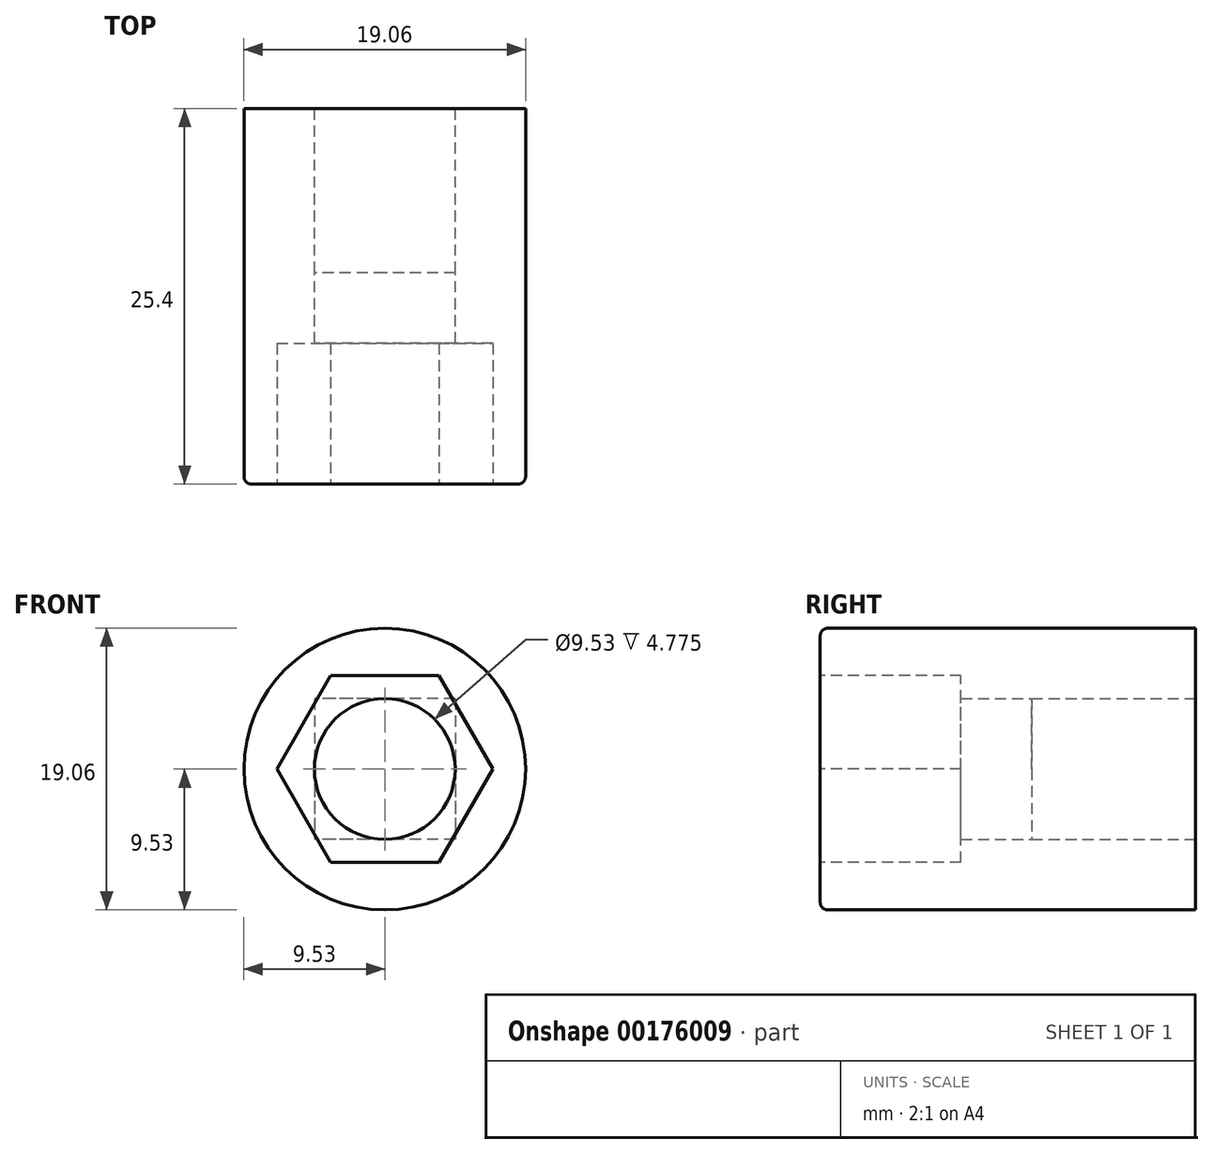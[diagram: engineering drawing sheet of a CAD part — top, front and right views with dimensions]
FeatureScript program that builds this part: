
annotation { "Feature Type Name" : "Feature", "Feature Type Description" : "" }
export const myFeature = defineFeature(function(context is Context, id is Id, definition is map)
    precondition{}
    {
        {
            var Q0;
            Q0=qCreatedBy(makeId("Front.planeOp"),FACE);
            var sketch = newSketch(context, id + "F0", { "sketchPlane" : qUnion([Q0])});
            skCircle(sketch, "E0", {"center": v(0, 0) * mm, "radius": 9.53 * mm});
            skSolve(sketch);
        }
        {
            var Q0;
            Q0=makeQuery(id+"F0.imprint","IMPRINT",FACE,{"disambiguationData":[TD([[makeQuery(id+"F0.imprint","IMPRINT",EDGE,{"derivedFrom":sQuery(id+"F0.wireOp",EDGE,"E0")}),1.0]])]});
            extrude(context, id + "F1", {"entities" : qUnion([Q0]), "depth" : 25.4 * mm});
        }
        {
            var Q0;
            Q0=qCreatedBy(makeId("Front.planeOp"),FACE);
            var sketch = newSketch(context, id + "F2", { "sketchPlane" : qUnion([Q0])});
            skLineSegment(sketch, "E1.bottom", {"start": v(4.76, 4.76) * mm, "end": v(-4.76, 4.76) * mm});
            skLineSegment(sketch, "E1.top", {"start": v(4.76, -4.76) * mm, "end": v(-4.76, -4.76) * mm});
            skLineSegment(sketch, "E1.left", {"start": v(4.76, 4.76) * mm, "end": v(4.76, -4.76) * mm});
            skLineSegment(sketch, "E1.right", {"start": v(-4.76, 4.76) * mm, "end": v(-4.76, -4.76) * mm});
            skPoint(sketch, "E1.middle", {"position": v(0, 0) * mm});
            skCircle(sketch, "E2", {"center": v(0, 0) * mm, "radius": 4.76 * mm});
            skSolve(sketch);
        }
        {
            var Q0;
            {var subQ0=sQuery(id+"F2.wireOp",EDGE,"E2");var subQ1=makeQuery(id+"F2.imprint","INTERSECT",VERTEX,{"derivedFrom":[sQuery(id+"F2.wireOp",EDGE,"E1.bottom"),subQ0]});Q0=makeQuery(id+"F2.imprint","IMPRINT",FACE,{"disambiguationData":[TD([[makeQuery(id+"F2.imprint","IMPRINT",EDGE,{"disambiguationData":[TD([[subQ1,1.0]])],"derivedFrom":subQ0}),1.0]])]});}
            extrude(context, id + "F3", {"entities" : qUnion([Q0]), "operationType" : NewBodyOperationType.REMOVE, "endBound" : BoundingType.THROUGH_ALL, "oppositeDirection" : true, "depth" : 25.4 * mm});
        }
        {
            var Q0;
            Q0=makeQuery(id+"F1.opExtrude","CAP_FACE",FACE,{"disambiguationData":[OSD([sQuery(id+"F0.wireOp",EDGE,"E0")])],"isStart":true});
            var sketch = newSketch(context, id + "F4", { "sketchPlane" : qUnion([Q0])});
            skLineSegment(sketch, "E3.bottom", {"start": v(4.76, -4.76) * mm, "end": v(-4.76, -4.76) * mm});
            skLineSegment(sketch, "E3.top", {"start": v(4.76, 4.76) * mm, "end": v(-4.76, 4.76) * mm});
            skLineSegment(sketch, "E3.left", {"start": v(4.76, -4.76) * mm, "end": v(4.76, 4.76) * mm});
            skLineSegment(sketch, "E3.right", {"start": v(-4.76, -4.76) * mm, "end": v(-4.76, 4.76) * mm});
            skPoint(sketch, "E3.middle", {"position": v(0, 0) * mm});
            skCircle(sketch, "E4", {"center": v(0, 0) * mm, "radius": 4.76 * mm});
            skSolve(sketch);
        }
        {
            var Q0;
            {var subQ0=sQuery(id+"F4.wireOp",EDGE,"E4");var subQ1=makeQuery(id+"F4.imprint","INTERSECT",VERTEX,{"derivedFrom":[sQuery(id+"F4.wireOp",EDGE,"E3.top"),subQ0]});Q0=makeQuery(id+"F4.imprint","IMPRINT",FACE,{"disambiguationData":[TD([[makeQuery(id+"F4.imprint","IMPRINT",EDGE,{"disambiguationData":[TD([[subQ1,1.0]])],"derivedFrom":subQ0}),1.0]])]});}
            extrude(context, id + "F5", {"entities" : qUnion([Q0]), "operationType" : NewBodyOperationType.REMOVE, "endBound" : BoundingType.THROUGH_ALL, "oppositeDirection" : true, "depth" : 25.4 * mm});
        }
        {
            var Q0;
            Q0 = qSketchRegion(id + "F2", true);
            extrude(context, id + "F6", {"entities" : qUnion([Q0]), "operationType" : NewBodyOperationType.REMOVE, "oppositeDirection" : true, "depth" : 9.4 * mm});
        }
        {
            var Q0;
            Q0 = qSketchRegion(id + "F2", true);
            extrude(context, id + "F7", {"entities" : qUnion([Q0]), "operationType" : NewBodyOperationType.REMOVE, "oppositeDirection" : true, "depth" : 12.7 * mm});
        }
        {
            var Q0;
            Q0 = qSketchRegion(id + "F2", true);
            extrude(context, id + "F8", {"entities" : qUnion([Q0]), "operationType" : NewBodyOperationType.REMOVE, "depth" : 11.1 * mm});
        }
        {
            var Q0;
            Q0=makeQuery(id+"F1.opExtrude","CAP_FACE",FACE,{"disambiguationData":[OSD([sQuery(id+"F0.wireOp",EDGE,"E0")])],"isStart":false});
            var sketch = newSketch(context, id + "F9", { "sketchPlane" : qUnion([Q0])});
            skCircle(sketch, "E5.cCircle", {"center": v(0, 0) * mm, "radius": 6.32 * mm, "construction": true});
            skLineSegment(sketch, "E5.0", {"start": v(-3.65, 6.32) * mm, "end": v(3.65, 6.32) * mm});
            skLineSegment(sketch, "E5.1", {"start": v(3.65, 6.32) * mm, "end": v(7.3, 0) * mm});
            skLineSegment(sketch, "E5.2", {"start": v(7.3, 0) * mm, "end": v(3.65, -6.32) * mm});
            skLineSegment(sketch, "E5.3", {"start": v(3.65, -6.32) * mm, "end": v(-3.65, -6.32) * mm});
            skLineSegment(sketch, "E5.4", {"start": v(-3.65, -6.32) * mm, "end": v(-7.3, 0) * mm});
            skLineSegment(sketch, "E5.5", {"start": v(-7.3, 0) * mm, "end": v(-3.65, 6.32) * mm});
            skPoint(sketch, "E5.0.midPoint", {"position": v(0, 6.32) * mm});
            skSolve(sketch);
        }
        {
            var Q0;
            Q0 = qSketchRegion(id + "F9", true);
            extrude(context, id + "F10", {"entities" : qUnion([Q0]), "operationType" : NewBodyOperationType.REMOVE, "oppositeDirection" : true, "depth" : 9.52 * mm});
        }
        {
            var Q0;
            Q0=makeQuery(id+"F1.opExtrude","CAP_EDGE",EDGE,{"disambiguationData":[OSD([sQuery(id+"F0.wireOp",EDGE,"E0")])],"isStart":false});
            var Q1;
            Q1=makeQuery(id+"F10.boolean.opBoolean","COPY",EDGE,{"derivedFrom":makeQuery(id+"F10.opExtrude","CAP_EDGE",EDGE,{"disambiguationData":[OSD([sQuery(id+"F9.wireOp",EDGE,"E5.5")])],"isStart":true})});
            var Q2;
            Q2=makeQuery(id+"F10.boolean.opBoolean","COPY",EDGE,{"derivedFrom":makeQuery(id+"F10.opExtrude","CAP_EDGE",EDGE,{"disambiguationData":[OSD([sQuery(id+"F9.wireOp",EDGE,"E5.0")])],"isStart":true})});
            var Q3;
            Q3=makeQuery(id+"F10.boolean.opBoolean","COPY",EDGE,{"derivedFrom":makeQuery(id+"F10.opExtrude","CAP_EDGE",EDGE,{"disambiguationData":[OSD([sQuery(id+"F9.wireOp",EDGE,"E5.1")])],"isStart":true})});
            var Q4;
            Q4=makeQuery(id+"F10.boolean.opBoolean","COPY",EDGE,{"derivedFrom":makeQuery(id+"F10.opExtrude","CAP_EDGE",EDGE,{"disambiguationData":[OSD([sQuery(id+"F9.wireOp",EDGE,"E5.4")])],"isStart":true})});
            var Q5;
            Q5=makeQuery(id+"F10.boolean.opBoolean","COPY",EDGE,{"derivedFrom":makeQuery(id+"F10.opExtrude","CAP_EDGE",EDGE,{"disambiguationData":[OSD([sQuery(id+"F9.wireOp",EDGE,"E5.3")])],"isStart":true})});
            var Q6;
            Q6=makeQuery(id+"F10.boolean.opBoolean","COPY",EDGE,{"derivedFrom":makeQuery(id+"F10.opExtrude","CAP_EDGE",EDGE,{"disambiguationData":[OSD([sQuery(id+"F9.wireOp",EDGE,"E5.2")])],"isStart":true})});
            fillet(context, id + "F11", {"entities" : qUnion([Q0, Q1, Q2, Q3, Q4, Q5, Q6]), "radius" : 0.5 * mm, "tangentPropagation" : true, "allowEdgeOverflow" : false});
        }
    });
